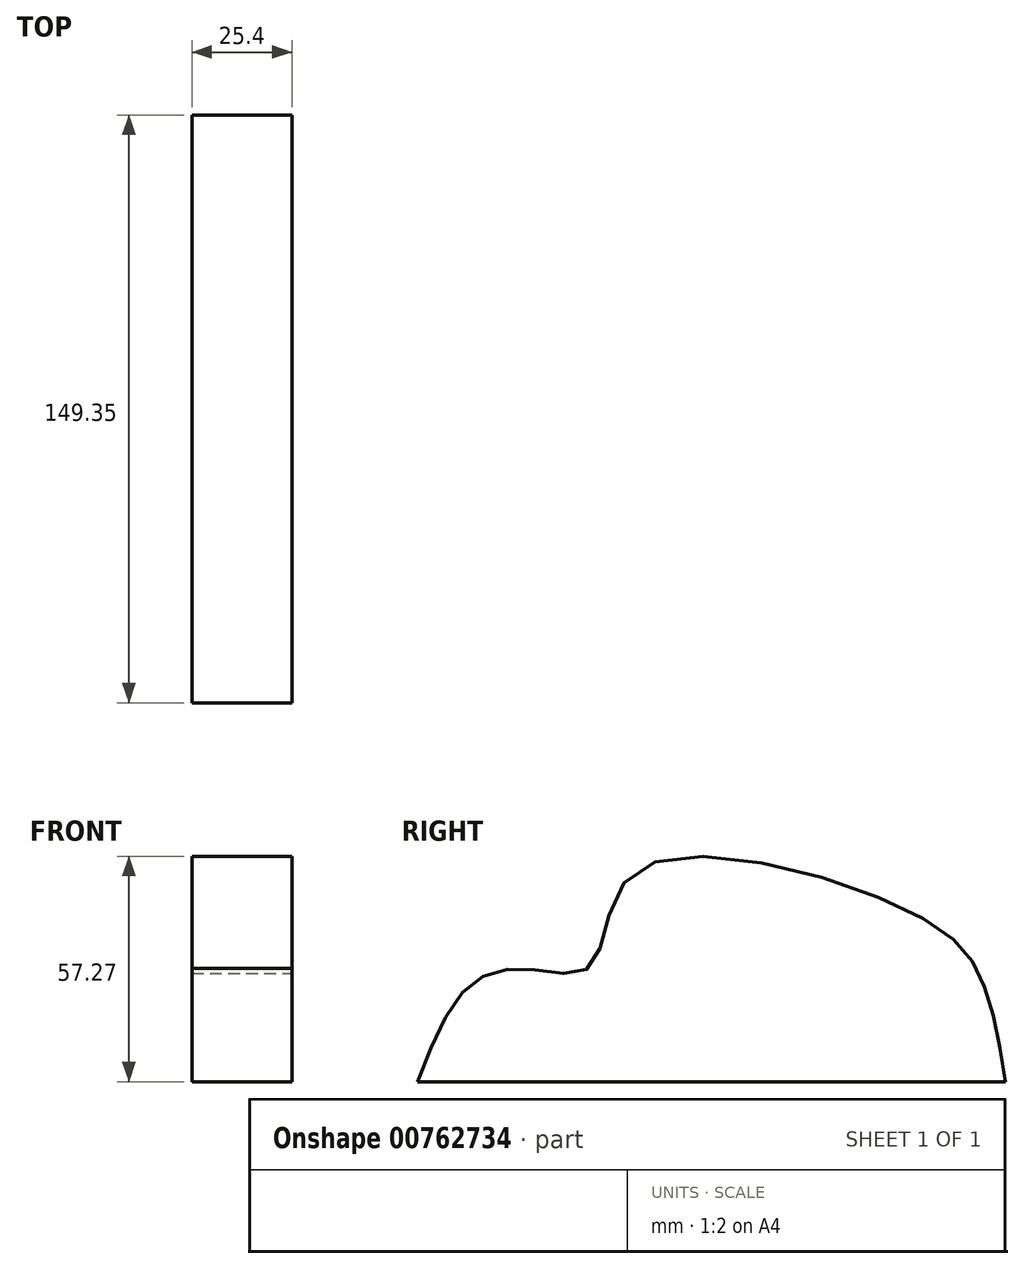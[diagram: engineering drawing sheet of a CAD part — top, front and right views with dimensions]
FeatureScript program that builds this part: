
annotation { "Feature Type Name" : "Feature", "Feature Type Description" : "" }
export const myFeature = defineFeature(function(context is Context, id is Id, definition is map)
    precondition{}
    {
        {
            var Q0;
            Q0=qCreatedBy(makeId("Right.planeOp"),FACE);
            var sketch = newSketch(context, id + "F0", { "sketchPlane" : qUnion([Q0])});
            skLineSegment(sketch, "E0", {"start": v(-74.52, 0) * mm, "end": v(74.83, 0) * mm});
            skFitSpline(sketch, "E1", {"points": [v(-74.52, 0) * mm, v(-62.03, 23.77) * mm, v(-46.79, 28.65) * mm, v(-30.63, 29.26) * mm, v(-19.35, 53.34) * mm, v(50.44, 43.28) * mm, v(69.04, 25.3) * mm, v(74.83, 0) * mm], "startDerivative": vector(76.53, 199.74) * mm, "endDerivative": vector(31.45, -197.46) * mm});
            skLineSegment(sketch, "E2", {"start": v(74.83, 0) * mm, "end": v(-74.52, 0) * mm});
            skSolve(sketch);
        }
        {
            var Q0;
            Q0 = qSketchRegion(id + "F0", true);
            extrude(context, id + "F1", {"entities" : qUnion([Q0]), "depth" : 25.4 * mm, "offsetDistance" : 25.4 * mm});
        }
    });
